# Revit family: KingswayGroup_MgntcLcks_Anti-LigatureMagLockHousing
name_source: partatom
category: Specialty Equipment
units: mm (PartAtom-declared; Revit-internal decimal feet)

## family parameters
Always vertical = Yes
Cut with Voids When Loaded = No
Part Type = Normal
Room Calculation Point = No
Round Connector Dimension = Use Diameter
Shared = No
Work Plane-Based = No

## types (1)
- KingswayGroup_MgntcLcks_Anti-LigatureMagLockHousing
    AssetType = Fixed
    BIMObjectName = KingswayGroup_MagneticLocks_Anti-LigatureMagLockHousing
    Category = Pr_75_30_27_50:Magnetic locks
    Color = For full range of available finishes and colours, contact Kingsway Group
    Default Elevation = 0 mm  [stored 0 ft]
    Description = Architectural Mag Lock Housing
    DurationUnit = year
    Features = A robust mag lock solution providing an overall holding force of 1200kg for use where security is a key consideration
    Finish = For full range of available finishes and colours, contact Kingsway Group
    HousingMaterial = NBS_Concept
    IfcExportAs = IfcDiscreteAccessoryType
    IfcExportType = USERDEFINED
    Length = 2040 mm  [stored 6.69291 ft]
    Manufacturer = Kingsway Group
    ManufacturerName = Kingsway Group
    ManufacturerURL = https://kingswaygroupglobal.com
    Material = For full range of available material, contact Kingsway Group
    Model = KG222
    ModelNumber = KG222
    ModelReference = Anti-Ligature Mag Lock Housing
    Name = MagneticLocks_Anti-LigatureMagLockHousing_KG222_KingswayGroup
    NominalHeight = 2040 mm  [stored 6.69291 ft]
    NominalLength = 125 mm  [stored 0.410105 ft]
    NominalWidth = 68 mm
    ProductInformation = https://kingswaygroupglobal.com
    Size = 125 x 2040 x 68 mm
    URL = https://kingswaygroupglobal.com
    Uniclass2015Code = Pr_75_30_27_50
    Uniclass2015Title = Magnetic locks
    Uniclass2015Version = Products v1.36
    Version = 1
    WarrantyDescription = 5-Year Guarantee *For faulty manufacture and not for damage
    WarrantyDurationParts = 5
    WarrantyDurationUnit = year

note: [stored X ft] marks values corroborated as IEEE doubles in the binary element streams (Revit-internal decimal feet)

## geometry (parser evidence)
native form markers: Sweep x2
no freeform markers — native parametric forms only
